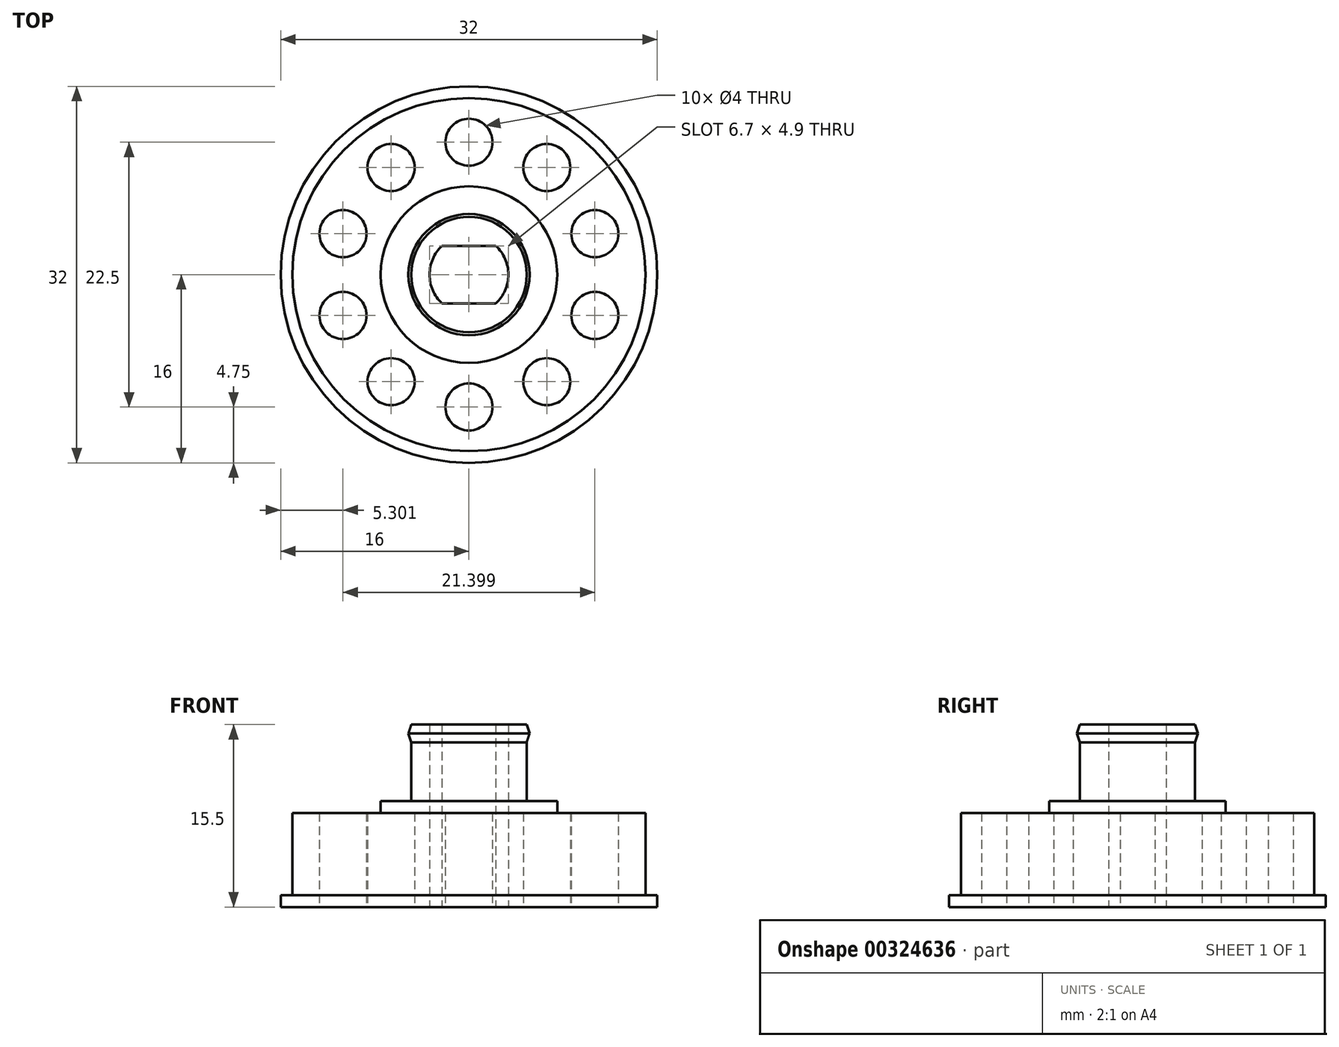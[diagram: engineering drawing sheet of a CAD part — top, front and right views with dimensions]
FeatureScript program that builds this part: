
annotation { "Feature Type Name" : "Feature", "Feature Type Description" : "" }
export const myFeature = defineFeature(function(context is Context, id is Id, definition is map)
    precondition{}
    {
        {
            assignVariable(context, id + "F0", {"name" : "e", "anyValue" : 6});
        }
        {
            assignVariable(context, id + "F1", {"name" : "h1", "anyValue" : 3});
        }
        {
            assignVariable(context, id + "F2", {"name" : "h2", "anyValue" : 6.5});
        }
        {
            var Q0;
            Q0=qCreatedBy(makeId("Top.planeOp"),FACE);
            var sketch = newSketch(context, id + "F3", { "sketchPlane" : qUnion([Q0])});
            skCircle(sketch, "E0", {"center": v(0, 0) * mm, "radius": 15 * mm});
            skCircle(sketch, "E1", {"center": v(0, 0) * mm, "radius": 7.5 * mm});
            skCircle(sketch, "E2", {"center": v(0, 0) * mm, "radius": 4.9 * mm});
            skArc(sketch, "E3", {"start": v(-2.28, 2.45) * mm, "mid": v(-3.35, 0) * mm, "end": v(-2.28, -2.45) * mm});
            skLineSegment(sketch, "E4.bottom", {"start": v(2.28, -2.45) * mm, "end": v(-2.28, -2.45) * mm});
            skLineSegment(sketch, "E4.top", {"start": v(2.28, 2.45) * mm, "end": v(-2.28, 2.45) * mm});
            skArc(sketch, "E5.trimOffspring", {"start": v(2.28, -2.45) * mm, "mid": v(3.35, 0) * mm, "end": v(2.28, 2.45) * mm});
            skPoint(sketch, "E6.orphan", {"position": v(3.35, 2.45) * mm});
            skPoint(sketch, "E7.orphan", {"position": v(3.35, -2.45) * mm});
            skPoint(sketch, "E8.orphan", {"position": v(-3.35, -2.45) * mm});
            skPoint(sketch, "E9.orphan", {"position": v(-3.35, 2.45) * mm});
            skLineSegment(sketch, "E10", {"start": v(0, 7.5) * mm, "end": v(0, 15) * mm, "construction": true});
            skPoint(sketch, "E10.endSnap0", {"position": v(0, 2.45) * mm});
            skCircle(sketch, "E11", {"center": v(0, 11.25) * mm, "radius": 2 * mm});
            skCircle(sketch, "E12.1.0", {"center": v(-6.61, 9.1) * mm, "radius": 2 * mm});
            skCircle(sketch, "E12.2.0", {"center": v(-10.7, 3.48) * mm, "radius": 2 * mm});
            skCircle(sketch, "E12.3.0", {"center": v(-10.7, -3.48) * mm, "radius": 2 * mm});
            skCircle(sketch, "E12.4.0", {"center": v(-6.61, -9.1) * mm, "radius": 2 * mm});
            skCircle(sketch, "E12.5.0", {"center": v(0, -11.25) * mm, "radius": 2 * mm});
            skCircle(sketch, "E12.6.0", {"center": v(6.61, -9.1) * mm, "radius": 2 * mm});
            skCircle(sketch, "E12.7.0", {"center": v(10.7, -3.48) * mm, "radius": 2 * mm});
            skCircle(sketch, "E12.8.0", {"center": v(10.7, 3.48) * mm, "radius": 2 * mm});
            skCircle(sketch, "E12.9.0", {"center": v(6.61, 9.1) * mm, "radius": 2 * mm});
            skCircle(sketch, "E13", {"center": v(0, 0) * mm, "radius": 16 * mm});
            skSolve(sketch);
        }
        {
            var Q0;
            Q0=makeQuery(id+"F3.imprint","IMPRINT",FACE,{"disambiguationData":[TD([[makeQuery(id+"F3.imprint","IMPRINT",EDGE,{"derivedFrom":sQuery(id+"F3.wireOp",EDGE,"E0")}),1.0]])]});
            var Q1;
            Q1=makeQuery(id+"F3.imprint","IMPRINT",FACE,{"disambiguationData":[TD([[makeQuery(id+"F3.imprint","IMPRINT",EDGE,{"derivedFrom":sQuery(id+"F3.wireOp",EDGE,"E1")}),1.0]])]});
            var Q2;
            Q2=makeQuery(id+"F3.imprint","IMPRINT",FACE,{"disambiguationData":[TD([[makeQuery(id+"F3.imprint","IMPRINT",EDGE,{"derivedFrom":sQuery(id+"F3.wireOp",EDGE,"E2")}),1.0]])]});
            extrude(context, id + "F4", {"entities" : qUnion([Q0, Q1, Q2]), "depth" : 8 * mm});
        }
        {
            var Q0;
            Q0=makeQuery(id+"F3.imprint","IMPRINT",FACE,{"disambiguationData":[TD([[makeQuery(id+"F3.imprint","IMPRINT",EDGE,{"derivedFrom":sQuery(id+"F3.wireOp",EDGE,"E1")}),1.0]])]});
            var Q1;
            Q1=makeQuery(id+"F3.imprint","IMPRINT",FACE,{"disambiguationData":[TD([[makeQuery(id+"F3.imprint","IMPRINT",EDGE,{"derivedFrom":sQuery(id+"F3.wireOp",EDGE,"E2")}),1.0]])]});
            extrude(context, id + "F5", {"entities" : qUnion([Q0, Q1]), "operationType" : NewBodyOperationType.ADD, "depth" : (getVariable(context, 'e') + getVariable(context, 'h1')) * mm});
        }
        {
            var Q0;
            Q0=makeQuery(id+"F3.imprint","IMPRINT",FACE,{"disambiguationData":[TD([[makeQuery(id+"F3.imprint","IMPRINT",EDGE,{"derivedFrom":sQuery(id+"F3.wireOp",EDGE,"E2")}),1.0]])]});
            extrude(context, id + "F6", {"entities" : qUnion([Q0]), "operationType" : NewBodyOperationType.ADD, "depth" : (getVariable(context, 'e') + getVariable(context, 'h1') + getVariable(context, 'h2')) * mm});
        }
        {
            var Q0;
            Q0=qCreatedBy(makeId("Front.planeOp"),FACE);
            var sketch = newSketch(context, id + "F7", { "sketchPlane" : qUnion([Q0])});
            skLineSegment(sketch, "E14", {"start": v(0, 0) * mm, "end": v(0, 17.5) * mm, "construction": true});
            skLineSegment(sketch, "E15", {"start": v(-4.9, 6) * mm, "end": v(-4.9, 12.5) * mm});
            skLineSegment(sketch, "E16", {"start": v(4.9, 15.5) * mm, "end": v(4.9, 6) * mm});
            skLineSegment(sketch, "E17.bottom", {"start": v(4.9, 15.5) * mm, "end": v(5.15, 15.5) * mm, "construction": true});
            skLineSegment(sketch, "E17.top", {"start": v(4.9, 14) * mm, "end": v(5.15, 14) * mm, "construction": true});
            skLineSegment(sketch, "E17.left", {"start": v(4.9, 15.5) * mm, "end": v(4.9, 14) * mm, "construction": true});
            skLineSegment(sketch, "E17.right", {"start": v(5.15, 15.5) * mm, "end": v(5.15, 14) * mm, "construction": true});
            skPoint(sketch, "E18", {"position": v(5.15, 14.75) * mm});
            skLineSegment(sketch, "E19", {"start": v(4.9, 15.5) * mm, "end": v(5.15, 14.75) * mm});
            skLineSegment(sketch, "E20", {"start": v(5.15, 14.75) * mm, "end": v(4.9, 14) * mm});
            skLineSegment(sketch, "E21", {"start": v(4.9, 14) * mm, "end": v(4.9, 15.5) * mm});
            skSolve(sketch);
        }
        {
            var Q0;
            Q0=makeQuery(id+"F7.imprint","IMPRINT",FACE,{"disambiguationData":[TD([[makeQuery(id+"F7.imprint","IMPRINT",EDGE,{"derivedFrom":sQuery(id+"F7.wireOp",EDGE,"E19")}),-1.0]])]});
            var Q1;
            Q1=sQuery(id+"F7.wireOp",EDGE,"E14");
            revolve(context, id + "F8", {"operationType" : NewBodyOperationType.ADD, "entities" : qUnion([Q0]), "axis" : qUnion([Q1]), "revolveType" : RevolveType.FULL});
        }
        {
            var Q0;
            Q0=makeQuery(id+"F6.opExtrude","CAP_FACE",FACE,{"disambiguationData":[OSD([sQuery(id+"F3.wireOp",EDGE,"E2"),sQuery(id+"F3.wireOp",EDGE,"E3"),sQuery(id+"F3.wireOp",EDGE,"E4.bottom"),sQuery(id+"F3.wireOp",EDGE,"E4.top"),sQuery(id+"F3.wireOp",EDGE,"E5.trimOffspring")])],"isStart":false});
            cPlane(context, id + "F9", {"entities" : qUnion([Q0]), "cplaneType" : CPlaneType.OFFSET, "offset" : 0 * mm, "width" : 150 * mm, "height" : 150 * mm});
        }
        {
            var Q0;
            Q0=qCreatedBy(id+"F9.planeOp",FACE);
            var sketch = newSketch(context, id + "F10", { "sketchPlane" : qUnion([Q0])});
            skArc(sketch, "E22", {"start": v(-2.38, 2.7) * mm, "mid": v(-3.6, 0) * mm, "end": v(-2.38, -2.7) * mm});
            skLineSegment(sketch, "E23.bottom", {"start": v(-2.38, 2.7) * mm, "end": v(2.38, 2.7) * mm});
            skLineSegment(sketch, "E23.top", {"start": v(-2.38, -2.7) * mm, "end": v(2.38, -2.7) * mm});
            skPoint(sketch, "E24.orphan", {"position": v(4.18, 2.7) * mm});
            skPoint(sketch, "E25.orphan", {"position": v(3.52, -2.7) * mm});
            skArc(sketch, "E26.trimOffspring", {"start": v(2.38, -2.7) * mm, "mid": v(3.6, 0) * mm, "end": v(2.38, 2.7) * mm});
            skPoint(sketch, "E27.orphan", {"position": v(-4.18, -2.7) * mm});
            skPoint(sketch, "E28.orphan", {"position": v(-3.52, 2.7) * mm});
            skSolve(sketch);
        }
        {
            var Q0;
            Q0=qSketchRegion(id+"F3",true);
            extrude(context, id + "F11", {"entities" : qUnion([Q0]), "operationType" : NewBodyOperationType.ADD, "depth" : 1 * mm});
        }
    });
